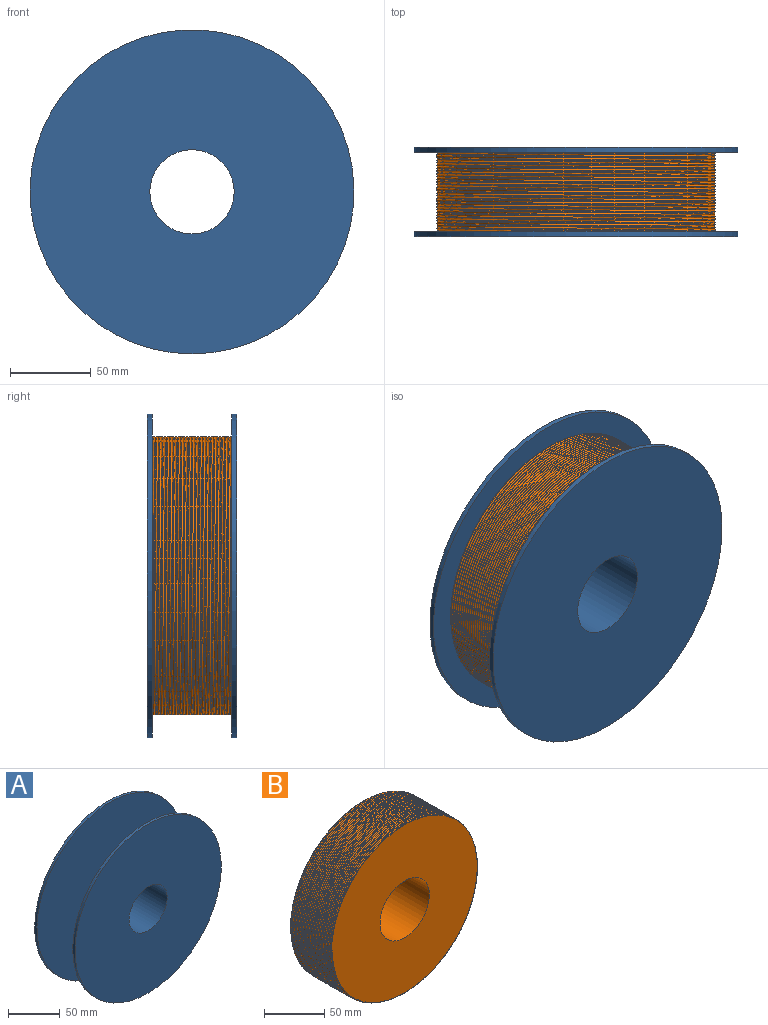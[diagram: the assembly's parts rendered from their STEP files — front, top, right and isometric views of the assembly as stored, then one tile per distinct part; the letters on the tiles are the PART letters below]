
ASSEMBLY  parts=2 mates=1
PART A: 8 faces, bbox 200x55x200 mm
  f0: cylinder r=100mm len=200mm, axis (0,1,0), area 1885mm2, adj f3,f6
  f1: cylinder r=100mm len=200mm, axis (0,1,0), area 1885mm2, adj f2,f5
  f2: plane 200x200mm, normal (0,-1,0), area 29292.2mm2, adj f1,f4
  f3: plane 200x200mm, normal (0,1,0), area 29292.2mm2, adj f0,f4
  f4: cylinder r=26mm len=55mm, axis (0,-1,0), area 8985mm2, adj f2,f3
  f5: plane 200x200mm, normal (0,1,0), area 28773.8mm2, adj f1,f7
  f6: plane 200x200mm, normal (0,-1,0), area 28773.8mm2, adj f0,f7
  f7: cylinder r=29mm len=58mm, axis (0,-1,0), area 8928.4mm2, adj f5,f6
PART B: 11 faces, bbox 173.8x50.7x196.6 mm
  f0: plane 0.89x0.87mm, normal (0,0,-1), area 0.6mm2, adj f3,f4,f8,f10
  f1: bspline ~170.99x170.39mm, area 17916.2mm2, adj f4,f7,f8,f10
  f2: plane 170.87x170.69mm, normal (0,1,0), area 20246.2mm2, adj f5,f6,f7,f9,f10
  f3: cylinder r=85mm len=169.58mm, axis (0,1,0), area 106.9mm2, adj f0,f4,f8
  f4: plane 171.09x170.77mm, normal (0,-1,0), area 20245.4mm2, adj f0,f1,f3,f5,f8
  f5: cylinder r=29mm len=58mm, axis (0,1,0), area 8928.4mm2, adj f2,f4
  f6: cylinder r=85mm len=161.09mm, axis (0,1,0), area 106.9mm2, adj f2,f7,f9
  f7: plane 0.87x0.8mm, normal (-0.9,0,0.45), area 0.6mm2, adj f1,f2,f6,f9
  f8: bspline ~172.18x170.42mm, area 54.9mm2, adj f0,f1,f3,f4
  f9: bspline ~174.48x173.12mm, area 54.9mm2, adj f2,f6,f7,f10
  f10: bspline ~170.99x170.39mm, area 17882mm2, adj f0,f1,f2,f9
PLACE A at identity
PLACE B at identity
MATE fastened B.f5 <-> A.f4  axis (0,1,0) through (0,0,0)mm
